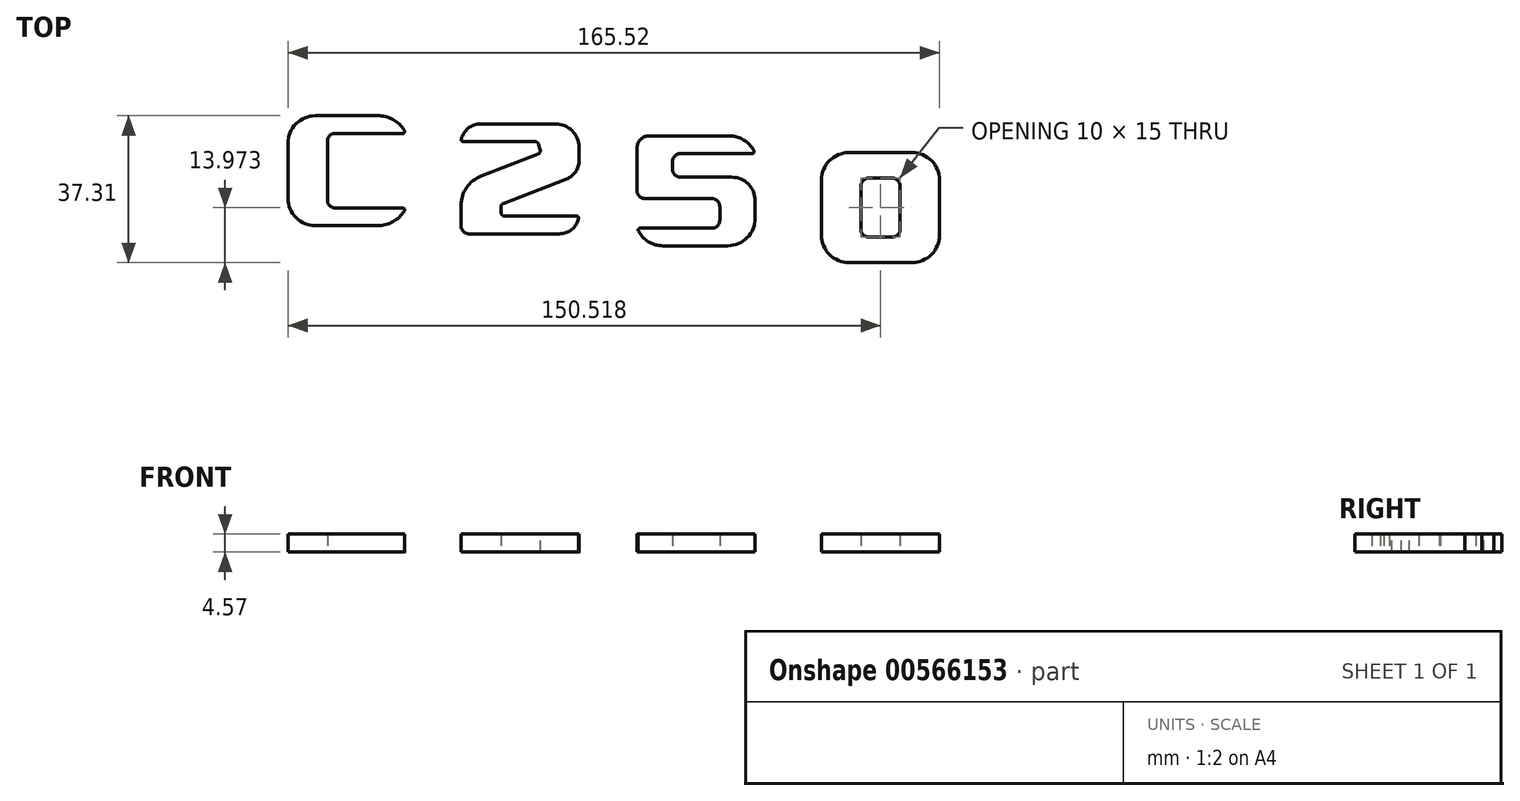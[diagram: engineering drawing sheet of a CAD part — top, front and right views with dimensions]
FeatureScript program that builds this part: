
annotation { "Feature Type Name" : "Feature", "Feature Type Description" : "" }
export const myFeature = defineFeature(function(context is Context, id is Id, definition is map)
    precondition{}
    {
        {
            var Q0;
            Q0=qCreatedBy(makeId("Top.planeOp"),FACE);
            var sketch = newSketch(context, id + "F0", { "sketchPlane" : qUnion([Q0])});
            skLineSegment(sketch, "E0", {"start": v(-24.08, 13.95) * mm, "end": v(-54.08, 13.95) * mm});
            skLineSegment(sketch, "E1", {"start": v(-54.08, 13.95) * mm, "end": v(-54.08, -13.99) * mm});
            skLineSegment(sketch, "E2", {"start": v(-54.08, -13.99) * mm, "end": v(-24.08, -13.99) * mm});
            skLineSegment(sketch, "E3", {"start": v(-44.08, 9.45) * mm, "end": v(-44.08, -9.49) * mm});
            skLineSegment(sketch, "E4", {"start": v(-44.08, 9.45) * mm, "end": v(-24.08, 9.45) * mm});
            skLineSegment(sketch, "E5", {"start": v(-24.08, 9.45) * mm, "end": v(-24.08, 13.95) * mm});
            skLineSegment(sketch, "E6", {"start": v(-44.08, -9.49) * mm, "end": v(-24.08, -9.49) * mm});
            skLineSegment(sketch, "E7", {"start": v(-24.08, -9.49) * mm, "end": v(-24.08, -13.99) * mm});
            skSolve(sketch);
        }
        {
            var Q0;
            Q0=makeQuery(id+"F0.imprint","IMPRINT",FACE,{"disambiguationData":[TD([[makeQuery(id+"F0.imprint","IMPRINT",EDGE,{"derivedFrom":sQuery(id+"F0.wireOp",EDGE,"E0")}),1.0]])]});
            extrude(context, id + "F1", {"entities" : qUnion([Q0]), "depth" : 4.57 * mm, "offsetDistance" : 25 * mm});
        }
        {
            var Q0;
            Q0=makeQuery(id+"F1.opExtrude","SWEPT_EDGE",EDGE,{"disambiguationData":[OSD([sQuery(id+"F0.wireOp",EDGE,"E3"),sQuery(id+"F0.wireOp",EDGE,"E4")])]});
            var Q1;
            Q1=makeQuery(id+"F1.opExtrude","SWEPT_EDGE",EDGE,{"disambiguationData":[OSD([sQuery(id+"F0.wireOp",EDGE,"E3"),sQuery(id+"F0.wireOp",EDGE,"E6")])]});
            fillet(context, id + "F2", {"entities" : qUnion([Q0, Q1]), "radius" : 2 * mm, "tangentPropagation" : true, "allowEdgeOverflow" : false});
        }
        {
            var Q0;
            Q0=makeQuery(id+"F1.opExtrude","SWEPT_EDGE",EDGE,{"disambiguationData":[OSD([sQuery(id+"F0.wireOp",EDGE,"E0"),sQuery(id+"F0.wireOp",EDGE,"E1")])]});
            var Q1;
            Q1=makeQuery(id+"F1.opExtrude","SWEPT_EDGE",EDGE,{"disambiguationData":[OSD([sQuery(id+"F0.wireOp",EDGE,"E1"),sQuery(id+"F0.wireOp",EDGE,"E2")])]});
            fillet(context, id + "F3", {"entities" : qUnion([Q0, Q1]), "radius" : 7 * mm, "tangentPropagation" : true, "allowEdgeOverflow" : false});
        }
        {
            var Q0;
            Q0=makeQuery(id+"F1.opExtrude","SWEPT_EDGE",EDGE,{"disambiguationData":[OSD([sQuery(id+"F0.wireOp",EDGE,"E2"),sQuery(id+"F0.wireOp",EDGE,"E7")])]});
            var Q1;
            Q1=makeQuery(id+"F1.opExtrude","SWEPT_EDGE",EDGE,{"disambiguationData":[OSD([sQuery(id+"F0.wireOp",EDGE,"E0"),sQuery(id+"F0.wireOp",EDGE,"E5")])]});
            fillet(context, id + "F4", {"entities" : qUnion([Q0, Q1]), "radius" : 8 * mm, "tangentPropagation" : true, "allowEdgeOverflow" : false});
        }
        {
            var Q0;
            Q0=makeQuery(id+"F4.opFillet","BLEND_EDGE",EDGE,{"blendedFrom":[makeQuery(id+"F1.opExtrude","SWEPT_EDGE",EDGE,{"disambiguationData":[OSD([sQuery(id+"F0.wireOp",EDGE,"E2"),sQuery(id+"F0.wireOp",EDGE,"E7")])]}),makeQuery(id+"F1.opExtrude","SWEPT_FACE",FACE,{"disambiguationData":[OSD([sQuery(id+"F0.wireOp",EDGE,"E6")])]})],"blendedInto":[makeQuery(id+"F1.opExtrude","SWEPT_FACE",FACE,{"disambiguationData":[OSD([sQuery(id+"F0.wireOp",EDGE,"E6")])]})]});
            var Q1;
            Q1=makeQuery(id+"F4.opFillet","BLEND_EDGE",EDGE,{"blendedFrom":[makeQuery(id+"F1.opExtrude","SWEPT_EDGE",EDGE,{"disambiguationData":[OSD([sQuery(id+"F0.wireOp",EDGE,"E0"),sQuery(id+"F0.wireOp",EDGE,"E5")])]}),makeQuery(id+"F1.opExtrude","SWEPT_FACE",FACE,{"disambiguationData":[OSD([sQuery(id+"F0.wireOp",EDGE,"E4")])]})],"blendedInto":[makeQuery(id+"F1.opExtrude","SWEPT_FACE",FACE,{"disambiguationData":[OSD([sQuery(id+"F0.wireOp",EDGE,"E4")])]})]});
            fillet(context, id + "F5", {"entities" : qUnion([Q0, Q1]), "radius" : 0.5 * mm, "tangentPropagation" : true, "allowEdgeOverflow" : false});
        }
        {
            var Q0;
            Q0=qCreatedBy(makeId("Top.planeOp"),FACE);
            var sketch = newSketch(context, id + "F6", { "sketchPlane" : qUnion([Q0])});
            skLineSegment(sketch, "E8", {"start": v(-10.15, 11.88) * mm, "end": v(19.85, 11.88) * mm});
            skLineSegment(sketch, "E9", {"start": v(19.85, 11.88) * mm, "end": v(19.85, -0.9) * mm});
            skLineSegment(sketch, "E10", {"start": v(19.85, -0.9) * mm, "end": v(0, -8.56) * mm});
            skLineSegment(sketch, "E11", {"start": v(0, -8.56) * mm, "end": v(0, -11.56) * mm});
            skLineSegment(sketch, "E12", {"start": v(0, -11.56) * mm, "end": v(19.85, -11.56) * mm});
            skLineSegment(sketch, "E13", {"start": v(19.85, -11.56) * mm, "end": v(19.85, -16.06) * mm});
            skLineSegment(sketch, "E14", {"start": v(-10.15, 11.88) * mm, "end": v(-10.15, 7.38) * mm});
            skLineSegment(sketch, "E15", {"start": v(-10.15, 7.38) * mm, "end": v(9.39, 7.38) * mm});
            skLineSegment(sketch, "E16", {"start": v(9.39, 7.38) * mm, "end": v(10.25, 4.5) * mm});
            skLineSegment(sketch, "E17", {"start": v(10.25, 4.5) * mm, "end": v(-10.12, -3.33) * mm});
            skLineSegment(sketch, "E18", {"start": v(-10.12, -3.33) * mm, "end": v(-10.12, -16.06) * mm});
            skLineSegment(sketch, "E19", {"start": v(-10.12, -16.06) * mm, "end": v(19.85, -16.06) * mm});
            skSolve(sketch);
        }
        {
            var Q0;
            Q0 = qSketchRegion(id + "F6", true);
            extrude(context, id + "F7", {"entities" : qUnion([Q0]), "depth" : 4.57 * mm, "offsetDistance" : 25 * mm});
        }
        {
            var Q0;
            Q0=makeQuery(id+"F7.opExtrude","SWEPT_EDGE",EDGE,{"disambiguationData":[OSD([sQuery(id+"F6.wireOp",EDGE,"E13"),sQuery(id+"F6.wireOp",EDGE,"E19")])]});
            var Q1;
            Q1=makeQuery(id+"F7.opExtrude","SWEPT_EDGE",EDGE,{"disambiguationData":[OSD([sQuery(id+"F6.wireOp",EDGE,"E8"),sQuery(id+"F6.wireOp",EDGE,"E14")])]});
            fillet(context, id + "F8", {"entities" : qUnion([Q0, Q1]), "radius" : 5 * mm, "tangentPropagation" : true, "allowEdgeOverflow" : false});
        }
        {
            var Q0;
            Q0=makeQuery(id+"F7.opExtrude","SWEPT_EDGE",EDGE,{"disambiguationData":[OSD([sQuery(id+"F6.wireOp",EDGE,"E9"),sQuery(id+"F6.wireOp",EDGE,"E10")])]});
            fillet(context, id + "F9", {"entities" : qUnion([Q0]), "radius" : 5 * mm, "tangentPropagation" : true, "allowEdgeOverflow" : false});
        }
        {
            var Q0;
            Q0=makeQuery(id+"F7.opExtrude","SWEPT_EDGE",EDGE,{"disambiguationData":[OSD([sQuery(id+"F6.wireOp",EDGE,"E15"),sQuery(id+"F6.wireOp",EDGE,"E16")])]});
            var Q1;
            Q1=makeQuery(id+"F7.opExtrude","SWEPT_EDGE",EDGE,{"disambiguationData":[OSD([sQuery(id+"F6.wireOp",EDGE,"E16"),sQuery(id+"F6.wireOp",EDGE,"E17")])]});
            var Q2;
            Q2=makeQuery(id+"F7.opExtrude","SWEPT_EDGE",EDGE,{"disambiguationData":[OSD([sQuery(id+"F6.wireOp",EDGE,"E10"),sQuery(id+"F6.wireOp",EDGE,"E11")])]});
            var Q3;
            Q3=makeQuery(id+"F7.opExtrude","SWEPT_EDGE",EDGE,{"disambiguationData":[OSD([sQuery(id+"F6.wireOp",EDGE,"E11"),sQuery(id+"F6.wireOp",EDGE,"E12")])]});
            fillet(context, id + "F10", {"entities" : qUnion([Q0, Q1, Q2, Q3]), "radius" : 1 * mm, "tangentPropagation" : true, "allowEdgeOverflow" : false});
        }
        {
            var Q0;
            Q0=makeQuery(id+"F8.opFillet","BLEND_EDGE",EDGE,{"blendedFrom":[makeQuery(id+"F7.opExtrude","SWEPT_EDGE",EDGE,{"disambiguationData":[OSD([sQuery(id+"F6.wireOp",EDGE,"E8"),sQuery(id+"F6.wireOp",EDGE,"E14")])]}),makeQuery(id+"F7.opExtrude","SWEPT_FACE",FACE,{"disambiguationData":[OSD([sQuery(id+"F6.wireOp",EDGE,"E15")])]})],"blendedInto":[makeQuery(id+"F7.opExtrude","SWEPT_FACE",FACE,{"disambiguationData":[OSD([sQuery(id+"F6.wireOp",EDGE,"E15")])]})]});
            var Q1;
            Q1=makeQuery(id+"F8.opFillet","BLEND_EDGE",EDGE,{"blendedFrom":[makeQuery(id+"F7.opExtrude","SWEPT_EDGE",EDGE,{"disambiguationData":[OSD([sQuery(id+"F6.wireOp",EDGE,"E13"),sQuery(id+"F6.wireOp",EDGE,"E19")])]}),makeQuery(id+"F7.opExtrude","SWEPT_FACE",FACE,{"disambiguationData":[OSD([sQuery(id+"F6.wireOp",EDGE,"E12")])]})],"blendedInto":[makeQuery(id+"F7.opExtrude","SWEPT_FACE",FACE,{"disambiguationData":[OSD([sQuery(id+"F6.wireOp",EDGE,"E12")])]})]});
            fillet(context, id + "F11", {"entities" : qUnion([Q0, Q1]), "radius" : .5 * mm, "tangentPropagation" : true, "allowEdgeOverflow" : false});
        }
        {
            var Q0;
            Q0=makeQuery(id+"F7.opExtrude","SWEPT_EDGE",EDGE,{"disambiguationData":[OSD([sQuery(id+"F6.wireOp",EDGE,"E18"),sQuery(id+"F6.wireOp",EDGE,"E19")])]});
            fillet(context, id + "F12", {"entities" : qUnion([Q0]), "radius" : 2 * mm, "tangentPropagation" : true, "allowEdgeOverflow" : false});
        }
        {
            var Q0;
            Q0=makeQuery(id+"F7.opExtrude","SWEPT_EDGE",EDGE,{"disambiguationData":[OSD([sQuery(id+"F6.wireOp",EDGE,"E17"),sQuery(id+"F6.wireOp",EDGE,"E18")])]});
            fillet(context, id + "F13", {"entities" : qUnion([Q0]), "radius" : 8 * mm, "tangentPropagation" : true, "allowEdgeOverflow" : false});
        }
        {
            var Q0;
            Q0=makeQuery(id+"F7.opExtrude","SWEPT_EDGE",EDGE,{"disambiguationData":[OSD([sQuery(id+"F6.wireOp",EDGE,"E8"),sQuery(id+"F6.wireOp",EDGE,"E9")])]});
            fillet(context, id + "F14", {"entities" : qUnion([Q0]), "radius" : 6 * mm, "tangentPropagation" : true, "allowEdgeOverflow" : false});
        }
        {
            var Q0;
            Q0=qCreatedBy(makeId("Top.planeOp"),FACE);
            var sketch = newSketch(context, id + "F15", { "sketchPlane" : qUnion([Q0])});
            skLineSegment(sketch, "E20", {"start": v(64.6, 8.83) * mm, "end": v(34.6, 8.83) * mm});
            skLineSegment(sketch, "E21", {"start": v(34.6, 8.83) * mm, "end": v(34.6, -7.1) * mm});
            skLineSegment(sketch, "E22", {"start": v(34.6, -7.1) * mm, "end": v(55.6, -7.1) * mm});
            skLineSegment(sketch, "E23", {"start": v(55.6, -7.1) * mm, "end": v(55.6, -14.6) * mm});
            skLineSegment(sketch, "E24", {"start": v(55.6, -14.6) * mm, "end": v(34.6, -14.6) * mm});
            skLineSegment(sketch, "E25", {"start": v(34.6, -14.6) * mm, "end": v(34.6, -19.1) * mm});
            skLineSegment(sketch, "E26", {"start": v(34.6, -19.1) * mm, "end": v(64.6, -19.1) * mm});
            skLineSegment(sketch, "E27", {"start": v(64.6, -19.1) * mm, "end": v(64.6, -1.67) * mm});
            skLineSegment(sketch, "E28", {"start": v(64.6, -1.67) * mm, "end": v(43.6, -1.67) * mm});
            skLineSegment(sketch, "E29", {"start": v(43.6, -1.67) * mm, "end": v(43.6, 4.33) * mm});
            skLineSegment(sketch, "E30", {"start": v(43.6, 4.33) * mm, "end": v(64.6, 4.33) * mm});
            skLineSegment(sketch, "E31", {"start": v(64.6, 4.33) * mm, "end": v(64.6, 8.83) * mm});
            skSolve(sketch);
        }
        {
            var Q0;
            Q0 = qSketchRegion(id + "F15", true);
            extrude(context, id + "F16", {"entities" : qUnion([Q0]), "depth" : 4.57 * mm, "offsetDistance" : 25 * mm});
        }
        {
            var Q0;
            Q0=makeQuery(id+"F16.opExtrude","SWEPT_EDGE",EDGE,{"disambiguationData":[OSD([sQuery(id+"F15.wireOp",EDGE,"E25"),sQuery(id+"F15.wireOp",EDGE,"E26")])]});
            var Q1;
            Q1=makeQuery(id+"F16.opExtrude","SWEPT_EDGE",EDGE,{"disambiguationData":[OSD([sQuery(id+"F15.wireOp",EDGE,"E20"),sQuery(id+"F15.wireOp",EDGE,"E31")])]});
            fillet(context, id + "F17", {"entities" : qUnion([Q0, Q1]), "radius" : 7 * mm, "tangentPropagation" : true, "allowEdgeOverflow" : false});
        }
        {
            var Q0;
            Q0=makeQuery(id+"F17.opFillet","BLEND_EDGE",EDGE,{"blendedFrom":[makeQuery(id+"F16.opExtrude","SWEPT_EDGE",EDGE,{"disambiguationData":[OSD([sQuery(id+"F15.wireOp",EDGE,"E25"),sQuery(id+"F15.wireOp",EDGE,"E26")])]}),makeQuery(id+"F16.opExtrude","SWEPT_FACE",FACE,{"disambiguationData":[OSD([sQuery(id+"F15.wireOp",EDGE,"E24")])]})],"blendedInto":[makeQuery(id+"F16.opExtrude","SWEPT_FACE",FACE,{"disambiguationData":[OSD([sQuery(id+"F15.wireOp",EDGE,"E24")])]})]});
            var Q1;
            Q1=makeQuery(id+"F17.opFillet","BLEND_EDGE",EDGE,{"blendedFrom":[makeQuery(id+"F16.opExtrude","SWEPT_EDGE",EDGE,{"disambiguationData":[OSD([sQuery(id+"F15.wireOp",EDGE,"E20"),sQuery(id+"F15.wireOp",EDGE,"E31")])]}),makeQuery(id+"F16.opExtrude","SWEPT_FACE",FACE,{"disambiguationData":[OSD([sQuery(id+"F15.wireOp",EDGE,"E30")])]})],"blendedInto":[makeQuery(id+"F16.opExtrude","SWEPT_FACE",FACE,{"disambiguationData":[OSD([sQuery(id+"F15.wireOp",EDGE,"E30")])]})]});
            fillet(context, id + "F18", {"entities" : qUnion([Q0, Q1]), "radius" : .5 * mm, "tangentPropagation" : true, "allowEdgeOverflow" : false});
        }
        {
            var Q0;
            Q0=makeQuery(id+"F16.opExtrude","SWEPT_EDGE",EDGE,{"disambiguationData":[OSD([sQuery(id+"F15.wireOp",EDGE,"E22"),sQuery(id+"F15.wireOp",EDGE,"E23")])]});
            var Q1;
            Q1=makeQuery(id+"F16.opExtrude","SWEPT_EDGE",EDGE,{"disambiguationData":[OSD([sQuery(id+"F15.wireOp",EDGE,"E23"),sQuery(id+"F15.wireOp",EDGE,"E24")])]});
            var Q2;
            Q2=makeQuery(id+"F16.opExtrude","SWEPT_EDGE",EDGE,{"disambiguationData":[OSD([sQuery(id+"F15.wireOp",EDGE,"E28"),sQuery(id+"F15.wireOp",EDGE,"E29")])]});
            var Q3;
            Q3=makeQuery(id+"F16.opExtrude","SWEPT_EDGE",EDGE,{"disambiguationData":[OSD([sQuery(id+"F15.wireOp",EDGE,"E29"),sQuery(id+"F15.wireOp",EDGE,"E30")])]});
            fillet(context, id + "F19", {"entities" : qUnion([Q0, Q1, Q2, Q3]), "radius" : 2 * mm, "tangentPropagation" : true, "allowEdgeOverflow" : false});
        }
        {
            var Q0;
            Q0=makeQuery(id+"F16.opExtrude","SWEPT_EDGE",EDGE,{"disambiguationData":[OSD([sQuery(id+"F15.wireOp",EDGE,"E20"),sQuery(id+"F15.wireOp",EDGE,"E21")])]});
            fillet(context, id + "F20", {"entities" : qUnion([Q0]), "radius" : 3 * mm, "tangentPropagation" : true, "allowEdgeOverflow" : false});
        }
        {
            var Q0;
            Q0=makeQuery(id+"F16.opExtrude","SWEPT_EDGE",EDGE,{"disambiguationData":[OSD([sQuery(id+"F15.wireOp",EDGE,"E21"),sQuery(id+"F15.wireOp",EDGE,"E22")])]});
            fillet(context, id + "F21", {"entities" : qUnion([Q0]), "radius" : 2 * mm, "tangentPropagation" : true, "allowEdgeOverflow" : false});
        }
        {
            var Q0;
            Q0=makeQuery(id+"F16.opExtrude","SWEPT_EDGE",EDGE,{"disambiguationData":[OSD([sQuery(id+"F15.wireOp",EDGE,"E27"),sQuery(id+"F15.wireOp",EDGE,"E28")])]});
            fillet(context, id + "F22", {"entities" : qUnion([Q0]), "radius" : 6 * mm, "tangentPropagation" : true, "allowEdgeOverflow" : false});
        }
        {
            var Q0;
            Q0=makeQuery(id+"F16.opExtrude","SWEPT_EDGE",EDGE,{"disambiguationData":[OSD([sQuery(id+"F15.wireOp",EDGE,"E26"),sQuery(id+"F15.wireOp",EDGE,"E27")])]});
            fillet(context, id + "F23", {"entities" : qUnion([Q0]), "radius" : 7 * mm, "tangentPropagation" : true, "allowEdgeOverflow" : false});
        }
        {
            var Q0;
            Q0=qCreatedBy(makeId("Top.planeOp"),FACE);
            var sketch = newSketch(context, id + "F24", { "sketchPlane" : qUnion([Q0])});
            skLineSegment(sketch, "E32.bottom", {"start": v(81.44, 4.58) * mm, "end": v(111.44, 4.58) * mm});
            skLineSegment(sketch, "E32.top", {"start": v(81.44, -23.36) * mm, "end": v(111.44, -23.36) * mm});
            skLineSegment(sketch, "E32.left", {"start": v(81.44, 4.58) * mm, "end": v(81.44, -23.36) * mm});
            skLineSegment(sketch, "E32.right", {"start": v(111.44, 4.58) * mm, "end": v(111.44, -23.36) * mm});
            skLineSegment(sketch, "E33.bottom", {"start": v(91.44, -1.89) * mm, "end": v(101.44, -1.89) * mm});
            skLineSegment(sketch, "E33.top", {"start": v(91.44, -16.89) * mm, "end": v(101.44, -16.89) * mm});
            skLineSegment(sketch, "E33.left", {"start": v(91.44, -1.89) * mm, "end": v(91.44, -16.89) * mm});
            skLineSegment(sketch, "E33.right", {"start": v(101.44, -1.89) * mm, "end": v(101.44, -16.89) * mm});
            skSolve(sketch);
        }
        {
            var Q0;
            Q0=makeQuery(id+"F24.imprint","IMPRINT",FACE,{"disambiguationData":[TD([[makeQuery(id+"F24.imprint","IMPRINT",EDGE,{"derivedFrom":sQuery(id+"F24.wireOp",EDGE,"E32.bottom")}),-1.0]])]});
            extrude(context, id + "F25", {"entities" : qUnion([Q0]), "depth" : 4.57 * mm, "offsetDistance" : 25 * mm});
        }
        {
            var Q0;
            Q0=makeQuery(id+"F25.opExtrude","SWEPT_EDGE",EDGE,{"disambiguationData":[OSD([sQuery(id+"F24.wireOp",EDGE,"E32.top"),sQuery(id+"F24.wireOp",EDGE,"E32.left")])]});
            var Q1;
            Q1=makeQuery(id+"F25.opExtrude","SWEPT_EDGE",EDGE,{"disambiguationData":[OSD([sQuery(id+"F24.wireOp",EDGE,"E32.top"),sQuery(id+"F24.wireOp",EDGE,"E32.right")])]});
            var Q2;
            Q2=makeQuery(id+"F25.opExtrude","SWEPT_EDGE",EDGE,{"disambiguationData":[OSD([sQuery(id+"F24.wireOp",EDGE,"E32.bottom"),sQuery(id+"F24.wireOp",EDGE,"E32.right")])]});
            var Q3;
            Q3=makeQuery(id+"F25.opExtrude","SWEPT_EDGE",EDGE,{"disambiguationData":[OSD([sQuery(id+"F24.wireOp",EDGE,"E32.bottom"),sQuery(id+"F24.wireOp",EDGE,"E32.left")])]});
            fillet(context, id + "F26", {"entities" : qUnion([Q0, Q1, Q2, Q3]), "radius" : 7 * mm, "tangentPropagation" : true, "allowEdgeOverflow" : false});
        }
        {
            var Q0;
            Q0=makeQuery(id+"F25.opExtrude","SWEPT_EDGE",EDGE,{"disambiguationData":[OSD([sQuery(id+"F24.wireOp",EDGE,"E33.bottom"),sQuery(id+"F24.wireOp",EDGE,"E33.left")])]});
            var Q1;
            Q1=makeQuery(id+"F25.opExtrude","SWEPT_EDGE",EDGE,{"disambiguationData":[OSD([sQuery(id+"F24.wireOp",EDGE,"E33.bottom"),sQuery(id+"F24.wireOp",EDGE,"E33.right")])]});
            var Q2;
            Q2=makeQuery(id+"F25.opExtrude","SWEPT_EDGE",EDGE,{"disambiguationData":[OSD([sQuery(id+"F24.wireOp",EDGE,"E33.top"),sQuery(id+"F24.wireOp",EDGE,"E33.right")])]});
            var Q3;
            Q3=makeQuery(id+"F25.opExtrude","SWEPT_EDGE",EDGE,{"disambiguationData":[OSD([sQuery(id+"F24.wireOp",EDGE,"E33.top"),sQuery(id+"F24.wireOp",EDGE,"E33.left")])]});
            fillet(context, id + "F27", {"entities" : qUnion([Q0, Q1, Q2, Q3]), "radius" : 2 * mm, "tangentPropagation" : true, "allowEdgeOverflow" : false});
        }
    });
